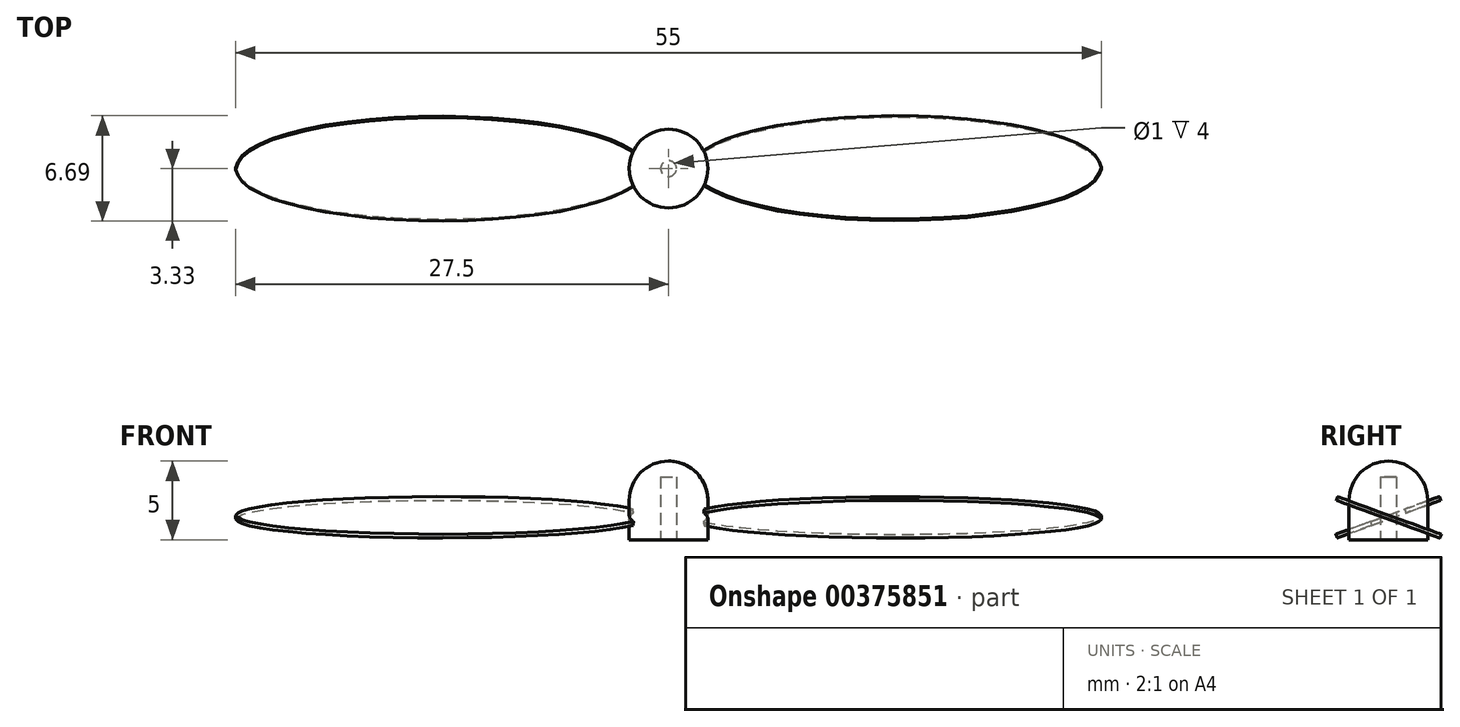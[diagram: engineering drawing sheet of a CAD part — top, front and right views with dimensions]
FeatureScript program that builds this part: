
annotation { "Feature Type Name" : "Feature", "Feature Type Description" : "" }
export const myFeature = defineFeature(function(context is Context, id is Id, definition is map)
    precondition{}
    {
        {
            var Q0;
            Q0=qCreatedBy(makeId("Front.planeOp"),FACE);
            var sketch = newSketch(context, id + "F0", { "sketchPlane" : qUnion([Q0])});
            skLineSegment(sketch, "E0", {"start": v(0, 0) * mm, "end": v(0, 5) * mm});
            skLineSegment(sketch, "E1", {"start": v(2.5, 0) * mm, "end": v(2.5, 2.5) * mm});
            skArc(sketch, "E2", {"start": v(0, 5) * mm, "mid": v(1.77, 4.27) * mm, "end": v(2.5, 2.5) * mm});
            skLineSegment(sketch, "E3", {"start": v(0, 0) * mm, "end": v(2.5, 0) * mm});
            skLineSegment(sketch, "E4", {"start": v(0.5, 0) * mm, "end": v(0.5, 4) * mm});
            skLineSegment(sketch, "E5", {"start": v(0.5, 4) * mm, "end": v(0, 4) * mm});
            skSolve(sketch);
        }
        {
            var Q0;
            {var subQ1=sQuery(id+"F0.wireOp",EDGE,"E1");Q0=makeQuery(id+"F0.imprint","IMPRINT",FACE,{"disambiguationData":[TD([[makeQuery(id+"F0.imprint","IMPRINT",EDGE,{"derivedFrom":subQ1}),1.0]])]});}
            var Q1;
            Q1=sQuery(id+"F0.wireOp",EDGE,"E0");
            revolve(context, id + "F1", {"entities" : qUnion([Q0]), "axis" : qUnion([Q1]), "revolveType" : RevolveType.FULL});
        }
        {
            var Q0;
            Q0=qCreatedBy(makeId("Right.planeOp"),FACE);
            var sketch = newSketch(context, id + "F2", { "sketchPlane" : qUnion([Q0])});
            skLineSegment(sketch, "E6", {"start": v(1.2, 1.87) * mm, "end": v(-1.2, 1) * mm});
            skLineSegment(sketch, "E7.0", {"start": v(1.12, 1.98) * mm, "end": v(-1.16, 1.15) * mm});
            skLineSegment(sketch, "E8.0", {"start": v(1.16, 1.73) * mm, "end": v(-1.12, 0.9) * mm});
            skLineSegment(sketch, "E9", {"start": v(-1.2, 0.96) * mm, "end": v(-1.2, 1.09) * mm});
            skLineSegment(sketch, "E10", {"start": v(1.2, 1.78) * mm, "end": v(1.2, 1.92) * mm});
            skPoint(sketch, "E11.visualSharp", {"position": v(1.2, 2) * mm});
            skArc(sketch, "E11.filletArc", {"start": v(1.2, 1.92) * mm, "mid": v(1.17, 1.97) * mm, "end": v(1.12, 1.98) * mm});
            skPoint(sketch, "E12.newPointB", {"position": v(1.2, 0) * mm});
            skArc(sketch, "E12.filletArc", {"start": v(1.16, 1.73) * mm, "mid": v(1.19, 1.75) * mm, "end": v(1.2, 1.78) * mm});
            skPoint(sketch, "E13.visualSharp", {"position": v(-1.2, 1.13) * mm});
            skArc(sketch, "E13.filletArc", {"start": v(-1.16, 1.15) * mm, "mid": v(-1.19, 1.13) * mm, "end": v(-1.2, 1.09) * mm});
            skPoint(sketch, "E14.newPointB", {"position": v(-1.2, 0) * mm});
            skArc(sketch, "E14.filletArc", {"start": v(-1.2, 0.96) * mm, "mid": v(-1.17, 0.9) * mm, "end": v(-1.12, 0.9) * mm});
            skLineSegment(sketch, "E15.MirrorCS", {"start": v(-1.12, 1.98) * mm, "end": v(1.16, 1.15) * mm});
            skLineSegment(sketch, "E16.MirrorCS", {"start": v(-1.2, 1.87) * mm, "end": v(1.2, 1) * mm});
            skLineSegment(sketch, "E17.MirrorCS", {"start": v(-1.16, 1.73) * mm, "end": v(1.12, 0.9) * mm});
            skLineSegment(sketch, "E18.MirrorCS", {"start": v(-1.2, 1.78) * mm, "end": v(-1.2, 1.92) * mm});
            skArc(sketch, "E19.MirrorCS", {"start": v(-1.2, 1.92) * mm, "mid": v(-1.17, 1.97) * mm, "end": v(-1.12, 1.98) * mm});
            skArc(sketch, "E20.MirrorCS", {"start": v(-1.16, 1.73) * mm, "mid": v(-1.19, 1.75) * mm, "end": v(-1.2, 1.78) * mm});
            skArc(sketch, "E21.MirrorCS", {"start": v(1.2, 0.96) * mm, "mid": v(1.17, 0.9) * mm, "end": v(1.12, 0.9) * mm});
            skLineSegment(sketch, "E22.MirrorCS", {"start": v(1.2, 0.96) * mm, "end": v(1.2, 1.09) * mm});
            skArc(sketch, "E23.MirrorCS", {"start": v(1.16, 1.15) * mm, "mid": v(1.19, 1.13) * mm, "end": v(1.2, 1.09) * mm});
            skSolve(sketch);
        }
        {
            var Q0;
            Q0=sQuery(id+"F2.wireOp",EDGE,"E6");
            var Q1;
            Q1=qCreatedBy(makeId("Top.planeOp"),FACE);
            cPlane(context, id + "F3", {"entities" : qUnion([Q0, Q1]), "cplaneType" : CPlaneType.LINE_ANGLE, "offset" : 25 * mm, "angle" : 0 * degree, "width" : 150 * mm, "height" : 150 * mm});
        }
        {
            var Q0;
            Q0=sQuery(id+"F2.wireOp",EDGE,"E16.MirrorCS");
            var Q1;
            Q1=qCreatedBy(makeId("Top.planeOp"),FACE);
            cPlane(context, id + "F4", {"entities" : qUnion([Q0, Q1]), "cplaneType" : CPlaneType.LINE_ANGLE, "offset" : 25 * mm, "angle" : 0 * degree, "width" : 150 * mm, "height" : 150 * mm});
        }
        {
            var Q0;
            Q0=qCreatedBy(id+"F3.planeOp",FACE);
            var sketch = newSketch(context, id + "F5", { "sketchPlane" : qUnion([Q0])});
            skLineSegment(sketch, "E24", {"start": v(0, -0.49) * mm, "end": v(-27.5, -0.49) * mm});
            skLineSegment(sketch, "E25", {"start": v(0, -0.49) * mm, "end": v(-0.75, -0.49) * mm});
            skLineSegment(sketch, "E26", {"start": v(-14.5, -0.49) * mm, "end": v(-14.5, -3.99) * mm});
            skEllipse(sketch, "E27", {"center": v(-14.5, -0.49) * mm, "majorRadius": 13 * mm, "minorRadius": 3.5 * mm, "majorAxis": v(-1, 0)});
            skSolve(sketch);
        }
        {
            var Q0;
            Q0 = qSketchRegion(id + "F5", true);
            extrude(context, id + "F6", {"entities" : qUnion([Q0]), "operationType" : NewBodyOperationType.ADD, "depth" : 0.25 * mm, "symmetric" : true});
        }
        {
            var Q0;
            Q0=qCreatedBy(id+"F4.planeOp",FACE);
            var sketch = newSketch(context, id + "F7", { "sketchPlane" : qUnion([Q0])});
            skLineSegment(sketch, "E28", {"start": v(0, 0.46) * mm, "end": v(27.5, 0.46) * mm});
            skLineSegment(sketch, "E29", {"start": v(14.5, 0.46) * mm, "end": v(14.5, 3.96) * mm});
            skEllipse(sketch, "E30", {"center": v(14.5, 0.46) * mm, "majorRadius": 13 * mm, "minorRadius": 3.5 * mm, "majorAxis": v(1, 0)});
            skSolve(sketch);
        }
        {
            var Q0;
            {var subQ0=sQuery(id+"F7.wireOp",EDGE,"E28");var subQ1=makeQuery(id+"F7.imprint","INTERSECT",VERTEX,{"derivedFrom":[subQ0,sQuery(id+"F7.wireOp",EDGE,"E29")]});Q0=makeQuery(id+"F7.imprint","IMPRINT",FACE,{"disambiguationData":[TD([[makeQuery(id+"F7.imprint","IMPRINT",EDGE,{"disambiguationData":[TD([[subQ1,1.0]])],"derivedFrom":subQ0}),-1.0]])]});}
            var Q1;
            {var subQ0=sQuery(id+"F7.wireOp",EDGE,"E29");Q1=makeQuery(id+"F7.imprint","IMPRINT",FACE,{"disambiguationData":[TD([[makeQuery(id+"F7.imprint","IMPRINT",EDGE,{"derivedFrom":subQ0}),1.0]])]});}
            var Q2;
            {var subQ3=sQuery(id+"F7.wireOp",EDGE,"E29");Q2=makeQuery(id+"F7.imprint","IMPRINT",FACE,{"disambiguationData":[TD([[makeQuery(id+"F7.imprint","IMPRINT",EDGE,{"derivedFrom":subQ3}),-1.0]])]});}
            extrude(context, id + "F8", {"entities" : qUnion([Q0, Q1, Q2]), "operationType" : NewBodyOperationType.ADD, "depth" : 0.25 * mm, "symmetric" : true});
        }
    });
